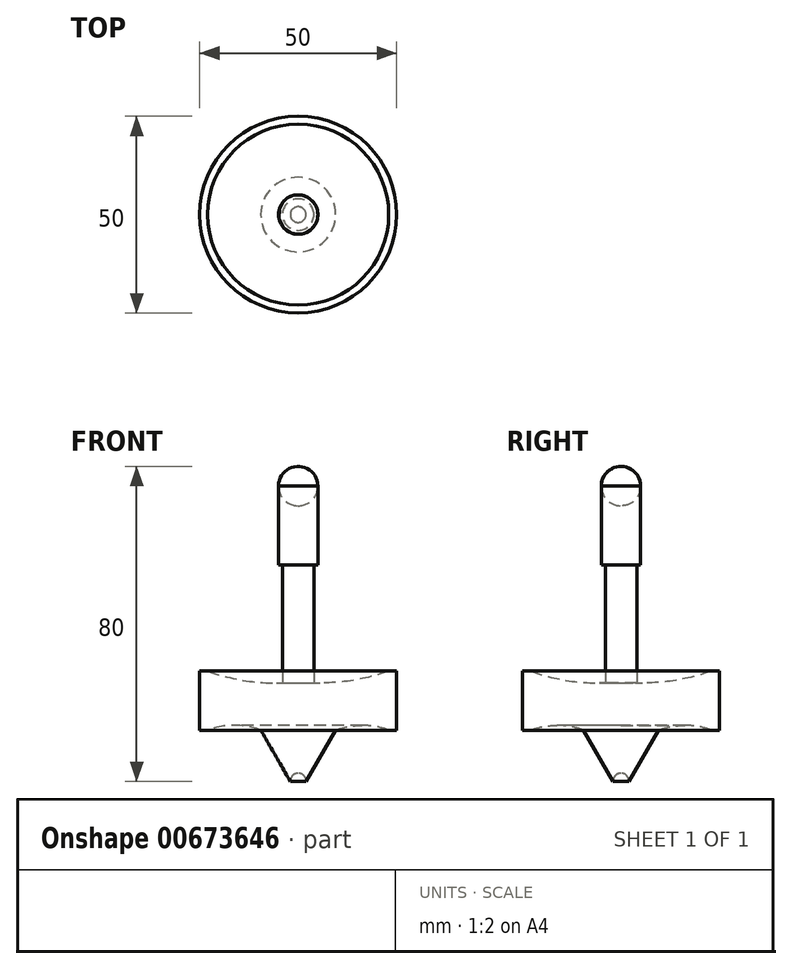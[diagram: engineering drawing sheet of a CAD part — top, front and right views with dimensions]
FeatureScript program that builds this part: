
annotation { "Feature Type Name" : "Feature", "Feature Type Description" : "" }
export const myFeature = defineFeature(function(context is Context, id is Id, definition is map)
    precondition{}
    {
        {
            var Q0;
            Q0=qCreatedBy(makeId("Right.planeOp"),FACE);
            var sketch = newSketch(context, id + "F0", { "sketchPlane" : qUnion([Q0])});
            skLineSegment(sketch, "E0", {"start": v(0, 0) * mm, "end": v(0, 55) * mm});
            skCircle(sketch, "E1", {"center": v(0, 0) * mm, "radius": 2 * mm, "construction": true});
            skLineSegment(sketch, "E2", {"start": v(0, -2) * mm, "end": v(0, 13) * mm});
            skLineSegment(sketch, "E3.left", {"start": v(-25, 13) * mm, "end": v(-25, 25) * mm});
            skLineSegment(sketch, "E4", {"start": v(-2, 0) * mm, "end": v(-9.5, 13) * mm});
            skLineSegment(sketch, "E5", {"start": v(-25, 13) * mm, "end": v(-23, 13) * mm});
            skArc(sketch, "E6", {"start": v(-9.5, 13) * mm, "mid": v(-16.25, 14.22) * mm, "end": v(-23, 13) * mm});
            skLineSegment(sketch, "E7.right", {"start": v(-5, 75.1) * mm, "end": v(-5, 55) * mm});
            skArc(sketch, "E8", {"start": v(0, 80) * mm, "mid": v(-3.57, 78.5) * mm, "end": v(-5, 74.9) * mm});
            skLineSegment(sketch, "E9", {"start": v(0, 55) * mm, "end": v(0, 80) * mm});
            skLineSegment(sketch, "E10", {"start": v(-4, 55) * mm, "end": v(-5, 55) * mm});
            skArc(sketch, "E11", {"start": v(0, 2.07) * mm, "mid": v(-1.44, 1.46) * mm, "end": v(-2, 0) * mm});
            skLineSegment(sketch, "E12", {"start": v(-4, 55) * mm, "end": v(-4, 25) * mm});
            skLineSegment(sketch, "E13", {"start": v(-25, 13) * mm, "end": v(-25, 28) * mm});
            skLineSegment(sketch, "E14", {"start": v(-23, 28) * mm, "end": v(-25, 28) * mm});
            skArc(sketch, "E15", {"start": v(-23, 28) * mm, "mid": v(-13.64, 25.62) * mm, "end": v(-4, 25) * mm});
            skPoint(sketch, "E16.orphan", {"position": v(2, 0) * mm});
            skSolve(sketch);
        }
        {
            var Q0;
            {var subQ6=sQuery(id+"F0.wireOp",EDGE,"E0");Q0=makeQuery(id+"F0.imprint","IMPRINT",FACE,{"disambiguationData":[TD([[makeQuery(id+"F0.imprint","IMPRINT",EDGE,{"derivedFrom":subQ6}),1.0]])]});}
            var Q1;
            Q1=sQuery(id+"F0.wireOp",EDGE,"E0");
            revolve(context, id + "F1", {"entities" : qUnion([Q0]), "axis" : qUnion([Q1]), "revolveType" : RevolveType.FULL});
        }
    });
